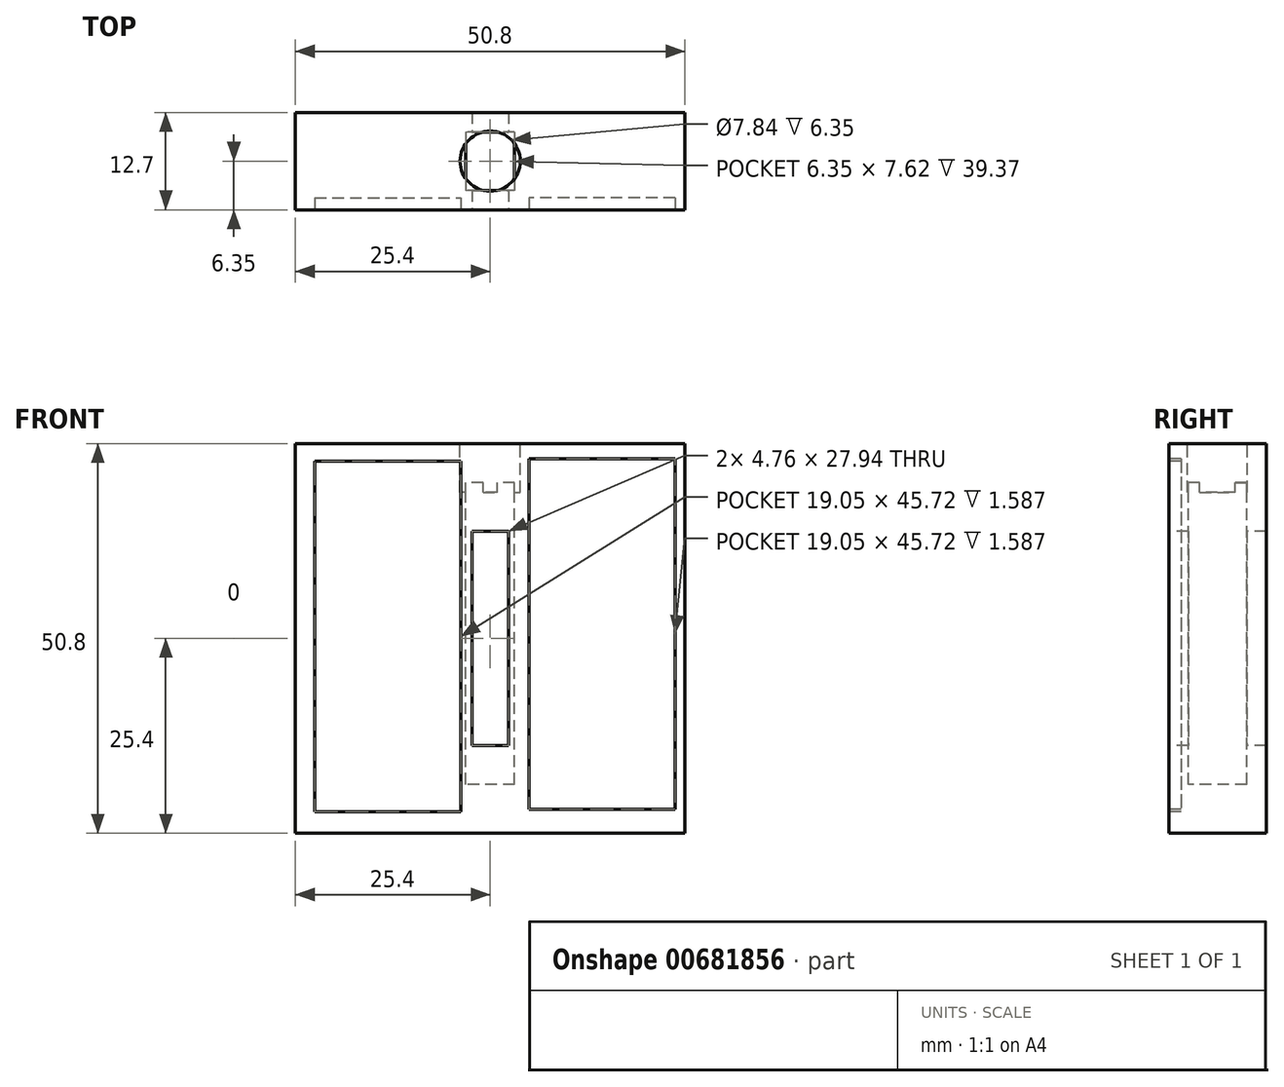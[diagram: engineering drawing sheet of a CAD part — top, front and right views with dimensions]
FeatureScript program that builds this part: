
annotation { "Feature Type Name" : "Feature", "Feature Type Description" : "" }
export const myFeature = defineFeature(function(context is Context, id is Id, definition is map)
    precondition{}
    {
        {
            var Q0;
            Q0=qCreatedBy(makeId("Top.planeOp"),FACE);
            var sketch = newSketch(context, id + "F0", { "sketchPlane" : qUnion([Q0])});
            skLineSegment(sketch, "E0.bottom", {"start": v(25.4, 6.35) * mm, "end": v(-25.4, 6.35) * mm});
            skLineSegment(sketch, "E0.top", {"start": v(25.4, -6.35) * mm, "end": v(-25.4, -6.35) * mm});
            skLineSegment(sketch, "E0.left", {"start": v(25.4, 6.35) * mm, "end": v(25.4, -6.35) * mm});
            skLineSegment(sketch, "E0.right", {"start": v(-25.4, 6.35) * mm, "end": v(-25.4, -6.35) * mm});
            skPoint(sketch, "E0.middle", {"position": v(0, 0) * mm});
            skSolve(sketch);
        }
        {
            var Q0;
            Q0=makeQuery(id+"F0.imprint","IMPRINT",FACE,{"disambiguationData":[TD([[makeQuery(id+"F0.imprint","IMPRINT",EDGE,{"derivedFrom":sQuery(id+"F0.wireOp",EDGE,"E0.bottom")}),1.0]])]});
            extrude(context, id + "F1", {"entities" : qUnion([Q0]), "depth" : 50.8 * mm, "offsetDistance" : 25.4 * mm});
        }
        {
            var Q0;
            Q0=makeQuery(id+"F1.opExtrude","CAP_FACE",FACE,{"disambiguationData":[OSD([sQuery(id+"F0.wireOp",EDGE,"E0.bottom"),sQuery(id+"F0.wireOp",EDGE,"E0.top"),sQuery(id+"F0.wireOp",EDGE,"E0.left"),sQuery(id+"F0.wireOp",EDGE,"E0.right")])],"isStart":false});
            var sketch = newSketch(context, id + "F2", { "sketchPlane" : qUnion([Q0])});
            skLineSegment(sketch, "E1.bottom", {"start": v(3.18, 3.81) * mm, "end": v(-3.18, 3.81) * mm});
            skLineSegment(sketch, "E1.top", {"start": v(3.18, -3.8) * mm, "end": v(-3.18, -3.8) * mm});
            skLineSegment(sketch, "E1.left", {"start": v(3.18, 3.81) * mm, "end": v(3.17, -3.8) * mm});
            skLineSegment(sketch, "E1.right", {"start": v(-3.18, 3.81) * mm, "end": v(-3.18, -3.8) * mm});
            skPoint(sketch, "E1.middle", {"position": v(0, 0) * mm});
            skSolve(sketch);
        }
        {
            var Q0;
            Q0=makeQuery(id+"F2.imprint","IMPRINT",FACE,{"disambiguationData":[TD([[makeQuery(id+"F2.imprint","IMPRINT",EDGE,{"derivedFrom":sQuery(id+"F2.wireOp",EDGE,"E1.bottom")}),1.0]])]});
            extrude(context, id + "F3", {"entities" : qUnion([Q0]), "operationType" : NewBodyOperationType.REMOVE, "oppositeDirection" : true, "depth" : 44.45 * mm, "offsetDistance" : 25.4 * mm, "hasSecondDirection" : true, "secondDirectionOppositeDirection" : true, "secondDirectionDepth" : 5.08 * mm});
        }
        {
            var Q0;
            Q0=makeQuery(id+"F1.opExtrude","CAP_FACE",FACE,{"disambiguationData":[OSD([sQuery(id+"F0.wireOp",EDGE,"E0.bottom"),sQuery(id+"F0.wireOp",EDGE,"E0.top"),sQuery(id+"F0.wireOp",EDGE,"E0.left"),sQuery(id+"F0.wireOp",EDGE,"E0.right")])],"isStart":false});
            var sketch = newSketch(context, id + "F4", { "sketchPlane" : qUnion([Q0])});
            skCircle(sketch, "E2", {"center": v(0, 0) * mm, "radius": 3.92 * mm});
            skSolve(sketch);
        }
        {
            var Q0;
            Q0 = qSketchRegion(id + "F4", true);
            extrude(context, id + "F5", {"entities" : qUnion([Q0]), "operationType" : NewBodyOperationType.REMOVE, "oppositeDirection" : true, "depth" : 6.35 * mm, "offsetDistance" : 25.4 * mm});
        }
        {
            var Q0;
            Q0=makeQuery(id+"F1.opExtrude","SWEPT_FACE",FACE,{"disambiguationData":[OSD([sQuery(id+"F0.wireOp",EDGE,"E0.top")])]});
            var sketch = newSketch(context, id + "F6", { "sketchPlane" : qUnion([Q0])});
            skLineSegment(sketch, "E3.bottom", {"start": v(2.38, 11.43) * mm, "end": v(-2.38, 11.43) * mm});
            skLineSegment(sketch, "E3.top", {"start": v(2.38, 39.37) * mm, "end": v(-2.38, 39.37) * mm});
            skLineSegment(sketch, "E3.left", {"start": v(2.38, 11.43) * mm, "end": v(2.38, 39.37) * mm});
            skLineSegment(sketch, "E3.right", {"start": v(-2.38, 11.43) * mm, "end": v(-2.38, 39.37) * mm});
            skPoint(sketch, "E3.middle", {"position": v(0, 25.4) * mm});
            skPoint(sketch, "E3.middle.positionSnap0", {"position": v(25.4, 25.4) * mm});
            skPoint(sketch, "E3.middle.positionSnap1", {"position": v(0, 50.8) * mm});
            skPoint(sketch, "E3.centerSnap0", {"position": v(25.4, 25.4) * mm});
            skPoint(sketch, "E3.centerSnap1", {"position": v(0, 50.8) * mm});
            skSolve(sketch);
        }
        {
            var Q0;
            Q0=makeQuery(id+"F6.imprint","IMPRINT",FACE,{"disambiguationData":[TD([[makeQuery(id+"F6.imprint","IMPRINT",EDGE,{"derivedFrom":sQuery(id+"F6.wireOp",EDGE,"E3.bottom")}),-1.0]])]});
            extrude(context, id + "F7", {"entities" : qUnion([Q0]), "operationType" : NewBodyOperationType.REMOVE, "endBound" : BoundingType.THROUGH_ALL, "oppositeDirection" : true, "depth" : 5.08 * mm, "offsetDistance" : 25.4 * mm});
        }
        {
            var Q0;
            Q0=makeQuery(id+"F1.opExtrude","SWEPT_FACE",FACE,{"disambiguationData":[OSD([sQuery(id+"F0.wireOp",EDGE,"E0.top")])]});
            var sketch = newSketch(context, id + "F8", { "sketchPlane" : qUnion([Q0])});
            skLineSegment(sketch, "E4.bottom", {"start": v(-22.86, 48.52) * mm, "end": v(-3.8, 48.52) * mm});
            skLineSegment(sketch, "E4.top", {"start": v(-22.86, 2.8) * mm, "end": v(-3.8, 2.8) * mm});
            skLineSegment(sketch, "E4.left", {"start": v(-22.86, 48.52) * mm, "end": v(-22.86, 2.8) * mm});
            skLineSegment(sketch, "E4.right", {"start": v(-3.8, 48.52) * mm, "end": v(-3.8, 2.8) * mm});
            skSolve(sketch);
        }
        {
            var Q0;
            Q0=makeQuery(id+"F8.imprint","IMPRINT",FACE,{"disambiguationData":[TD([[makeQuery(id+"F8.imprint","IMPRINT",EDGE,{"derivedFrom":sQuery(id+"F8.wireOp",EDGE,"E4.bottom")}),-1.0]])]});
            extrude(context, id + "F9", {"entities" : qUnion([Q0]), "operationType" : NewBodyOperationType.REMOVE, "oppositeDirection" : true, "depth" : 1.59 * mm, "offsetDistance" : 25.4 * mm});
        }
        {
            var Q0;
            Q0=makeQuery(id+"F1.opExtrude","SWEPT_FACE",FACE,{"disambiguationData":[OSD([sQuery(id+"F0.wireOp",EDGE,"E0.top")])]});
            var sketch = newSketch(context, id + "F10", { "sketchPlane" : qUnion([Q0])});
            skLineSegment(sketch, "E5.bottom", {"start": v(24.13, 48.81) * mm, "end": v(5.08, 48.81) * mm});
            skLineSegment(sketch, "E5.top", {"start": v(24.13, 3.1) * mm, "end": v(5.08, 3.1) * mm});
            skLineSegment(sketch, "E5.left", {"start": v(24.13, 48.81) * mm, "end": v(24.13, 3.1) * mm});
            skLineSegment(sketch, "E5.right", {"start": v(5.08, 48.81) * mm, "end": v(5.08, 3.1) * mm});
            skSolve(sketch);
        }
        {
            var Q0;
            Q0 = qSketchRegion(id + "F10", true);
            extrude(context, id + "F11", {"entities" : qUnion([Q0]), "operationType" : NewBodyOperationType.REMOVE, "oppositeDirection" : true, "depth" : 1.59 * mm, "offsetDistance" : 25.4 * mm});
        }
    });
